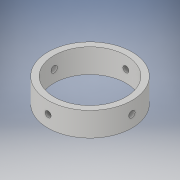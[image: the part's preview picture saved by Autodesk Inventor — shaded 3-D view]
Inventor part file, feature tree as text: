
AUTODESK INVENTOR PART (.ipt)
format: ipt  version: 2017 SP1 (Build 210196100, 196)  size: 128,000 bytes
history: native  units: in
note: dims shown in document units (in); Inventor stores cm internally (conversion verified against a paired STEP export)
features: sketch x3, plane x2, hole x2, extrude x1
ambient origin geometry x8: Origin, YZ Plane, XZ Plane, XY Plane, X Axis, Y Axis, Z Axis, Center Point
bodies: Solid1 (feature_tree)
feature tree (8):
  extrude  "Extrusion1"  Depth=3.5in
  plane  "Work Plane1"
  hole  "Hole1"  [1 undecoded]
  plane  "Work Plane2"
  hole  "Hole2"  [1 undecoded]
  sketch  "Sketch1"  dims[d0=3.0in d1=3.5in]
  sketch  "Sketch2"  dims[d2=1.0in d3=0.0in]
  sketch  "Sketch3"  dims[d4=1.75in d5=0.25in d6=0.75in d7=0.375in d8=0.25in d9=0.5635in d10=1.0in d11=0.8108in d12=1.75in d13=0.266in d14=0.75in d15=0.507in d16=0.25in d17=0.5635in d18=1.0in d19=0.8108in]
note: 2 required parameter values undecoded (feature->parameter linkage not recoverable at this tier; creation-order binding heuristic only, values carry confidence <= 0.55)
